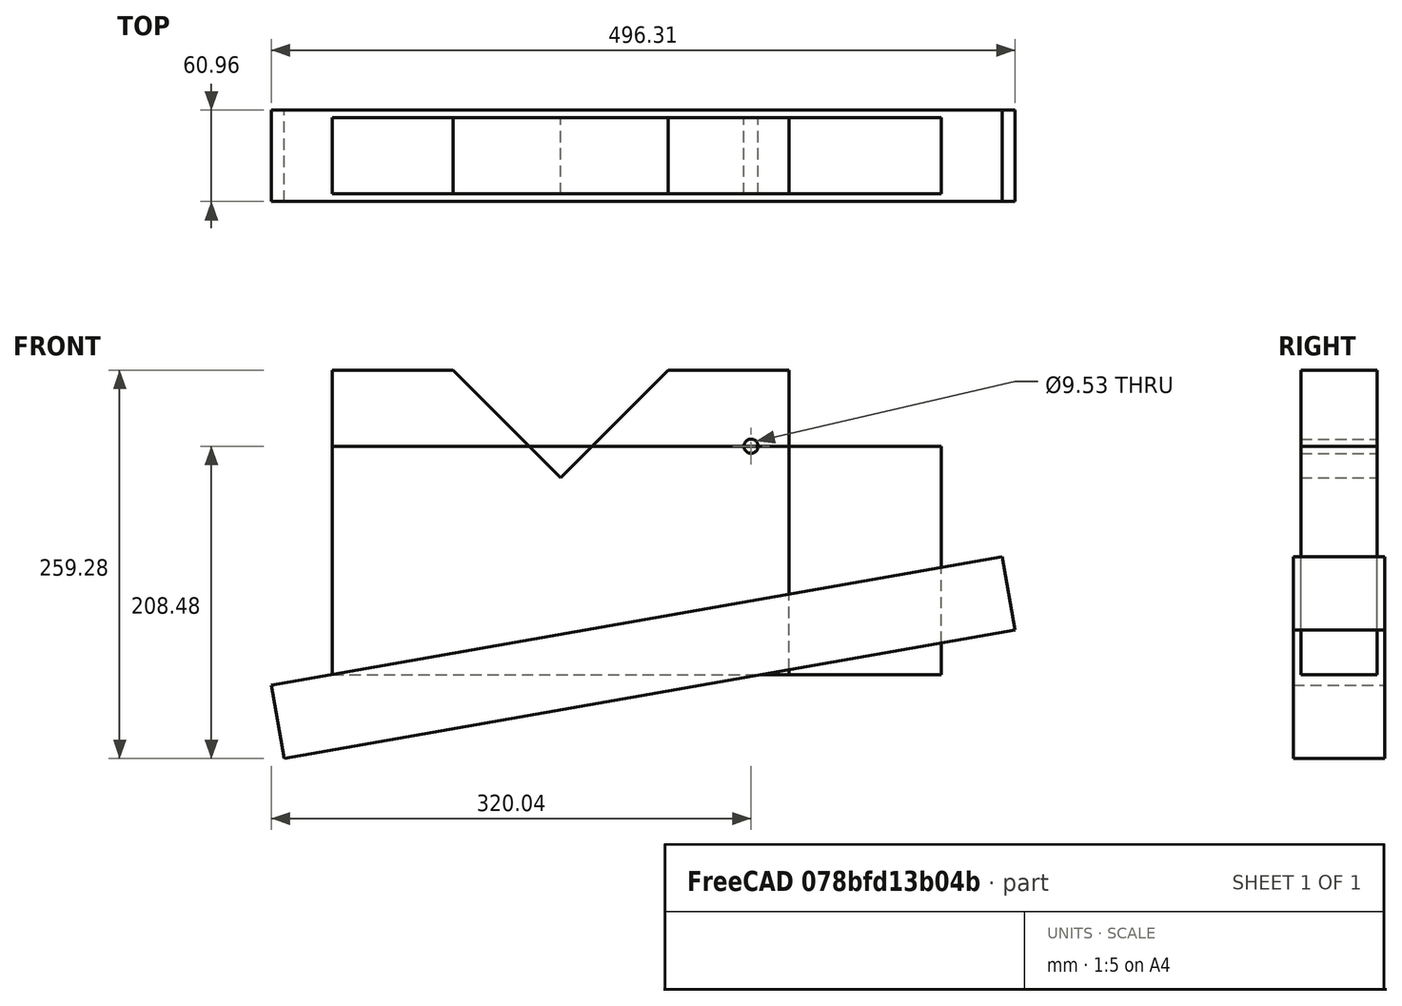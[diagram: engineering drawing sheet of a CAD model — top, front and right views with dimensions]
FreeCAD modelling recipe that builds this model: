
FCSTD DOCUMENT  (FreeCAD 0.17R7744 (Git))
Label: magnet_splitter
License: All rights reserved
LicenseURL: http://en.wikipedia.org/wiki/All_rights_reserved
objects: Part::Box×4, Part::Cut×2, Spreadsheet::Sheet×1, Part::Cylinder×1, App::DocumentObjectGroup×1, Part::Mirroring×1
note: 8 computed .brp shape members not serialized (recipe doc carries the construction recipe); baked Part::Feature solids carry a one-line shape summary decoded from their .brp

FEATURE [Part::Box] Box  label="Block"
  AttacherType = Attacher::AttachEngine3D
  Height = 203.2
  Length = 304.8
  Width = 50.8
  expr: Width = Parameters.block_thickness
  expr: Length = Parameters.anchor_length
  expr: Height = Parameters.block_height
FEATURE [Spreadsheet::Sheet] Spreadsheet  label="Parameters"
  cells = A1=Design Parameter; B1=Value; C1=Note; A3=Block Thickness; B3(block_thickness)==2in; C3=Thickness of wood block being used for construction; A4=Block Height; B4(block_height)==8in; C4=Height of block beign used for construction; A6=Anchor Length; B6(anchor_length)==12in; C6=Length of anchor block; A7=Handle Length; B7(handle_length)==16in; C7=Lenght of handle block; A8=Base Length; B8(base_length)==handle_length; C8=Length of the base block (can be built from excess wedge cut); A9=Base Width; B9(base_width)==wedge_offset; C9=Width of base block (can be built from excess of wedge cut); A11=Wedge Angle; B11(wedge_angle)=10; C11=Angle of cut for separation handle; A12=Wedge Offset; B12(wedge_offset)==0.25 * block_height; C12=Offset for angle to be cut on separation handle (for use of a signal block size); A13=Cutout Depth; B13(cutout_depth)==4in; C13=Depth of cutout on the anchor block; A14=Cutout Ratio X; B14(cutout_ratio_x)==1 / 2; C14=Ratio (along length of the anchor) for the placement of the center of the cutout; A15=Cutout Center; B15(cutout_center)==anchor_length * cutout_ratio_x; C15=Placement of the center of the anchor block cutout; A17=Bolt Ratio Y; B17(bolt_ratio_x)==3 / 4; C17=Ratio from bottom edge of block for bolt placement; A18=Bolt Position Y; B18(bolt_position_y)==block_height * bolt_ratio_x; C18=Actual position (computed from ratio); A19=Bolt Inset (X); B19(bolt_inset)==1in; C19=Distance from edge of block for bolt placement; A20=Bolt Diameter; B20(bolt_diameter)==3in / 8; C20=Diameter of bolt; A22=Maximum Magnet Size; C22=Largest magnet the separator can handle (based on cutout, wedge angle, and bolt placement); A23=Block Lenght; B23==anchor_length + handle_length; C23=Total length of wood block required for construction
FEATURE [Part::Box] Box001  label="Cutout"
  AttacherType = Attacher::AttachEngine3D
  Height = 111.76
  Length = 111.76
  Placement = pos=(152.4,-5.08,131.358) rot=(0,-1,0;0.785398rad)
  Width = 60.96
  expr: Placement.Base.z = Parameters.block_height - Parameters.cutout_depth / sqrt(2)
  expr: Placement.Base.x = Parameters.cutout_center
  expr: Height = Parameters.cutout_depth * 1.1
  expr: Length = Parameters.cutout_depth * 1.1
  expr: Placement.Base.y = -Parameters.block_thickness * 0.1
  expr: Width = Parameters.block_thickness * 1.2
FEATURE [Part::Cut] Cut
  Base = -> Box
  Tool = -> Box001
FEATURE [Part::Cylinder] Cylinder  label="Hole"
  Angle = 360
  AttacherType = Attacher::AttachEngine3D
  Height = 60.96
  Placement = pos=(279.4,-5.08,152.4) rot=(-1,0,0;1.5708rad)
  Radius = 4.7625
  expr: Placement.Base.z = Parameters.bolt_position_y
  expr: Placement.Base.y = -Parameters.block_thickness * 0.1
  expr: Placement.Base.x = Parameters.anchor_length - Spreadsheet.bolt_inset
  expr: Height = Parameters.block_thickness * 1.2
  expr: Radius = Parameters.bolt_diameter / 2
FEATURE [Part::Cut] Cut001  label="Anchor Block"
  Base = -> Cut
  Tool = -> Cylinder
FEATURE [App::DocumentObjectGroup] Group  label="Model"
  Group = -> [Cut001]
FEATURE [Part::Box] Box002  label="Block001"
  AttacherType = Attacher::AttachEngine3D
  Height = 152.4
  Length = 406.4
  Width = 50.8
  expr: Placement.Rotation.Angle = 0
  expr: Height = Parameters.block_height - Parameters.wedge_offset
  expr: Width = Parameters.block_thickness
  expr: Length = Parameters.handle_length
FEATURE [Part::Box] Box003  label="Wedge"
  AttacherType = Attacher::AttachEngine3D
  Height = 49.6711
  Length = 495.203
  Placement = pos=(-40.64,-5.08,7.16593) rot=(0,1,0;0.174533rad)
  Width = 60.96
  expr: Placement.Base.z = 0.1 * Parameters.handle_length * tan(Parameters.wedge_angle)
  expr: Height = 1.1 * Parameters.handle_length * Parameters.wedge_angle / 90
  expr: Placement.Base.x = -0.1 * Parameters.handle_length
  expr: Placement.Base.y = -0.1 * Parameters.block_thickness
  expr: Width = 1.2 * Parameters.block_thickness
  expr: Placement.Rotation.Angle = Parameters.wedge_angle
  expr: Length = 1.2 * Parameters.handle_length / cos(Parameters.wedge_angle)
FEATURE [Part::Mirroring] Part__Mirroring  label="Wedge (Mirror #1)"
  Base = (0,0,0)
  Normal = (0,0,1)
  Source = -> Box003
